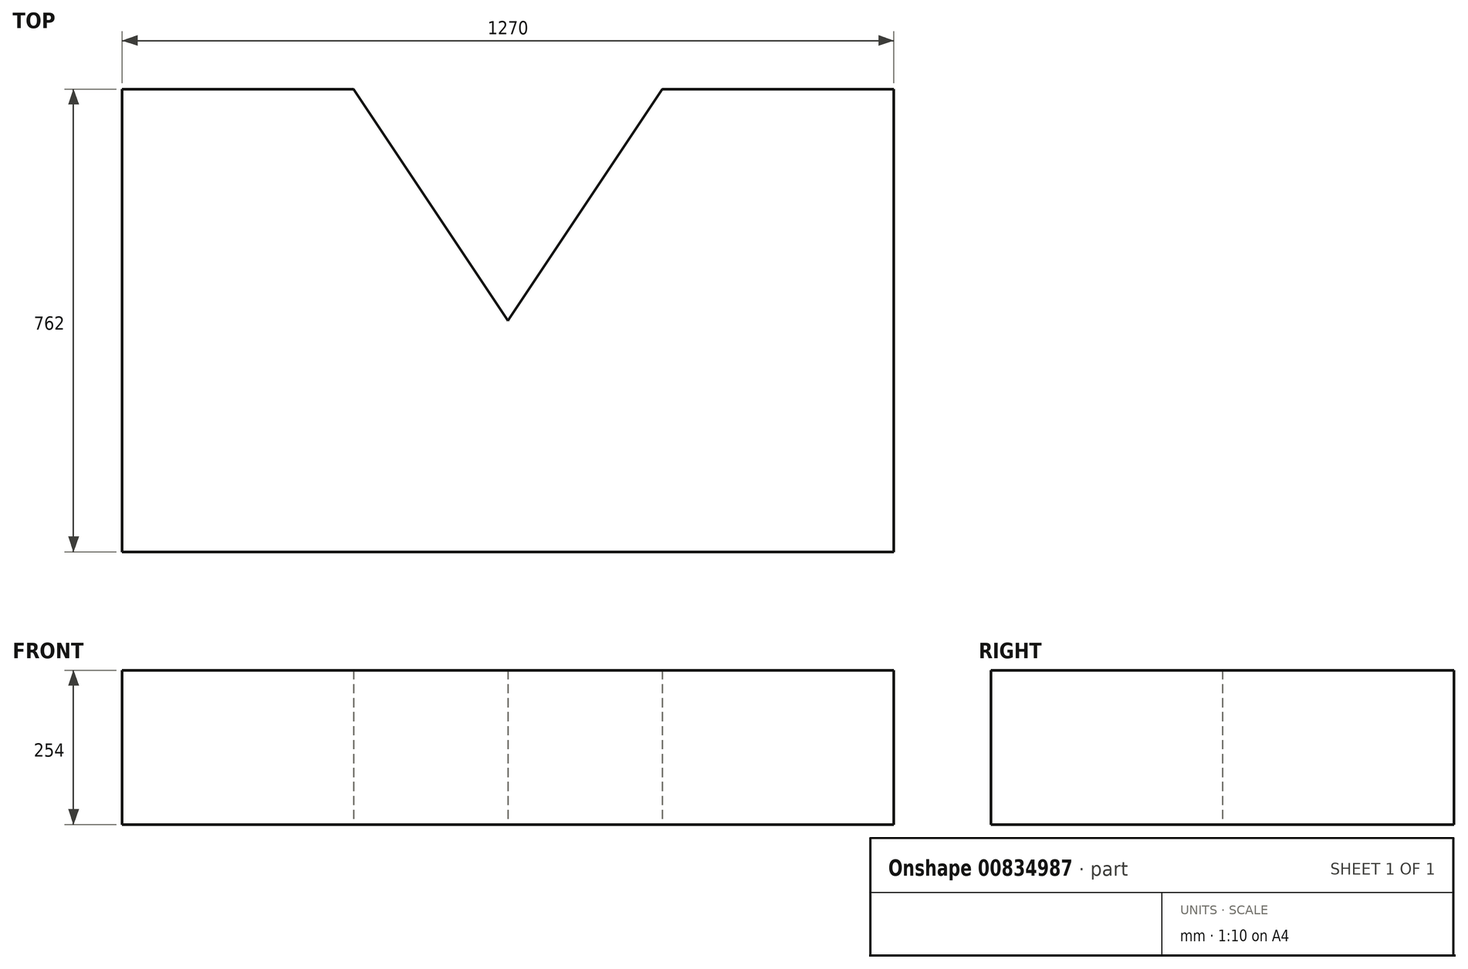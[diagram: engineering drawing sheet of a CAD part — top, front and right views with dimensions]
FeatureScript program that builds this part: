
annotation { "Feature Type Name" : "Feature", "Feature Type Description" : "" }
export const myFeature = defineFeature(function(context is Context, id is Id, definition is map)
    precondition{}
    {
        {
            var Q0;
            Q0=qCreatedBy(makeId("Top.planeOp"),FACE);
            var sketch = newSketch(context, id + "F0", { "sketchPlane" : qUnion([Q0])});
            skLineSegment(sketch, "E0", {"start": v(0, 381) * mm, "end": v(254, 762) * mm});
            skLineSegment(sketch, "E1", {"start": v(254, 762) * mm, "end": v(635, 762) * mm});
            skLineSegment(sketch, "E2", {"start": v(635, 762) * mm, "end": v(635, 0) * mm});
            skLineSegment(sketch, "E3", {"start": v(635, 0) * mm, "end": v(0, 0) * mm});
            skLineSegment(sketch, "E4.MirrorCS", {"start": v(0, 381) * mm, "end": v(-254, 762) * mm});
            skLineSegment(sketch, "E5.MirrorCS", {"start": v(-254, 762) * mm, "end": v(-635, 762) * mm});
            skLineSegment(sketch, "E6.MirrorCS", {"start": v(-635, 762) * mm, "end": v(-635, 0) * mm});
            skLineSegment(sketch, "E7.MirrorCS", {"start": v(-635, 0) * mm, "end": v(0, 0) * mm});
            skSolve(sketch);
        }
        {
            var Q0;
            Q0=makeQuery(id+"F0.imprint","IMPRINT",FACE,{"disambiguationData":[TD([[makeQuery(id+"F0.imprint","IMPRINT",EDGE,{"derivedFrom":sQuery(id+"F0.wireOp",EDGE,"E0")}),-1.0]])]});
            extrude(context, id + "F1", {"entities" : qUnion([Q0]), "depth" : 254 * mm, "offsetDistance" : 25.4 * mm});
        }
    });
